# Revit family: EN 280TJ STV
name_source: partatom
category: Equipement spécialisé
units: mm (PartAtom-declared; Revit-internal decimal feet)

## family parameters
Basée sur le plan de construction = Non
Cote de connecteur circulaire = Utiliser le diamètre
Couper avec des vides une fois chargée = Non
Numéro OmniClass = 23.50.00.00
Partagée = Non
Point de calcul de pièce = Non
Titre OmniClass = Conveying Systems & Material Handling
Toujours verticalement = Oui
Type d'élément = Normal

## types (1)
- 280TJ ST5
    Average consumption (L/h) = 2.38
    Average consumption (l/day) = 0 m
    CO2 emissions (g/kWh) = 6.3
    Commentaires du type = Nacelle élévatrice télescopique tout-terrain
    Counterweight offset (turret at 90°) = 1.43 m
    Créé par = ATLANCAD
    Elévation par défaut = 0 m
    Engine norm = Stage V
    External turning radius = 4.35 m
    Fabricant = MANITOU
    Floor height (access) = 0.4 m
    Ground clearance = 0.36 m
    Ground clearance at centre of wheelbase = 0.41 m
    I.C. Engine power rating - Power (ch) = 46
    I.C. Engine power rating - Power (kW) = 34.3
    Internal turning radius (over tyres) = 1.97 m
    Jib length = 4.3 m
    Max. lifting height = 27.73 m
    Max. outreach = 21.45 m
    Modèle = 280TJ ST5
    Noise to environment (LwA) = 102
    Number of people (inside) = 3
    Number of people (outside) = 2
    Overall height (stowed) = 2.71 m
    Overall height (transport) = 2.73 m
    Overall lenght (stowed) = 8.09 m
    Overall lenght (transport) = 11.36 m
    Permissible leveling = 4.00°
    Platform capacity = 350.00 kg
    Platform dimensions (length) = 2.3 m
    Platform dimensions (width) = 0.9 m
    Platform weight = 16500
    URL = www.manitou.com
    Wheelbase = 2.8 m
    Width = 2.48 m
